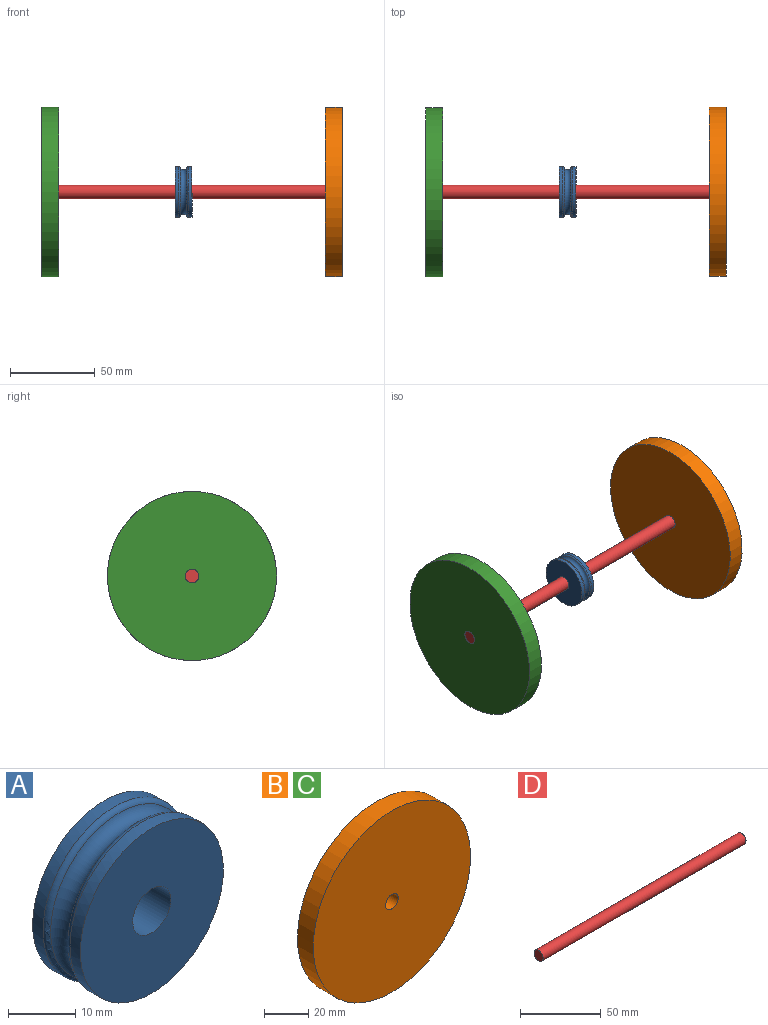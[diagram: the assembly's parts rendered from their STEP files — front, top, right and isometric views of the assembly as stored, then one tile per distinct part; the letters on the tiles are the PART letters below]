
ASSEMBLY  parts=4 mates=3
PART A: 8 faces, bbox 32.5x10x32.5 mm
  f0: plane 30x30mm, normal (0,1,0), area 656.6mm2, adj f1,f5
  f1: cylinder r=15mm len=30mm, axis (0,-1,0), area 204.7mm2, adj f0,f6
  f2: torus R=15mm, axis (0,-1,0), area 416.7mm2, adj f6,f7
  f3: cylinder r=15mm len=30mm, axis (0,-1,0), area 204.7mm2, adj f4,f7
  f4: plane 30x30mm, normal (0,-1,0), area 656.6mm2, adj f3,f5
  f5: cylinder r=4mm len=10mm, axis (0,-1,0), area 251.3mm2, adj f0,f4
  f6: torus R=14mm, axis (0,1,0), area 114.2mm2, adj f1,f2
  f7: torus R=14mm, axis (0,1,0), area 114.2mm2, adj f2,f3
PART B: 4 faces, bbox 100x10x100 mm
  f0: plane 100x100mm, normal (0,-1,0), area 7803.7mm2, adj f1,f3
  f1: cylinder r=4mm len=10mm, axis (0,-1,0), area 251.3mm2, adj f0,f2
  f2: plane 100x100mm, normal (0,1,0), area 7803.7mm2, adj f1,f3
  f3: cylinder r=50mm len=100mm, axis (0,-1,0), area 3141.6mm2, adj f0,f2
PART C: same geometry as B
PART D: 3 faces, bbox 177.8x8x8 mm
  f0: cylinder r=4mm len=177.8mm, axis (-1,0,0), area 4468.6mm2, adj f1,f2
  f1: plane 8x8mm, normal (1,0,0), area 50.3mm2, adj f0
  f2: plane 8x8mm, normal (-1,0,0), area 50.3mm2, adj f0
PLACE A rot(axis=(0.71,0.71,0),180deg) t=(-85.83,-19.22,4.09)mm
PLACE B rot(axis=(0.58,0.58,-0.58),120deg) t=(-1.93,-19.22,4.09)mm
PLACE C rot(axis=(-0.58,-0.58,-0.58),120deg) t=(-169.73,-19.22,4.09)mm
PLACE D t=(-80.83,-19.22,4.09)mm
MATE fastened C.f1 <-> D.f0  axis (-1,0,0) through (-169.73,-19.22,4.09)mm
MATE fastened A.f5 <-> D.f0  axis (1,0,0) through (-80.83,-19.22,4.09)mm
MATE fastened B.f1 <-> D.f0  axis (1,0,0) through (8.07,-19.22,4.09)mm
